AUTODESK INVENTOR PART (.ipt)
format: ipt  version: 2014 SP1 (Build 180222100, 222)  size: 96,256 bytes
history: native  units: in
note: dims shown in document units (in); Inventor stores cm internally (conversion verified against a paired STEP export)
features: sketch x1
ambient origin geometry x8: Origin, YZ Plane, XZ Plane, XY Plane, X Axis, Y Axis, Z Axis, Center Point
feature tree (1):
  sketch  "Sketch1"  dims[d0=22.0in d1=2.0in d2=6.0in d3=6.0in d4=1.5in d5=1.0in d6=0.5in d9=0.5in d10=0.5in d11=3.0in d50=1.0in d51=24.0in d52=0.5in d53=0.5in d54=0.5in d55=0.5in d56=21.5in d57=21.5in d58=7.65in d59=7.65in d60=6.0in d62=6.0in d65=18.0in d70=11.0in d71=25.0in d75=18.722in d76=24.0in]
